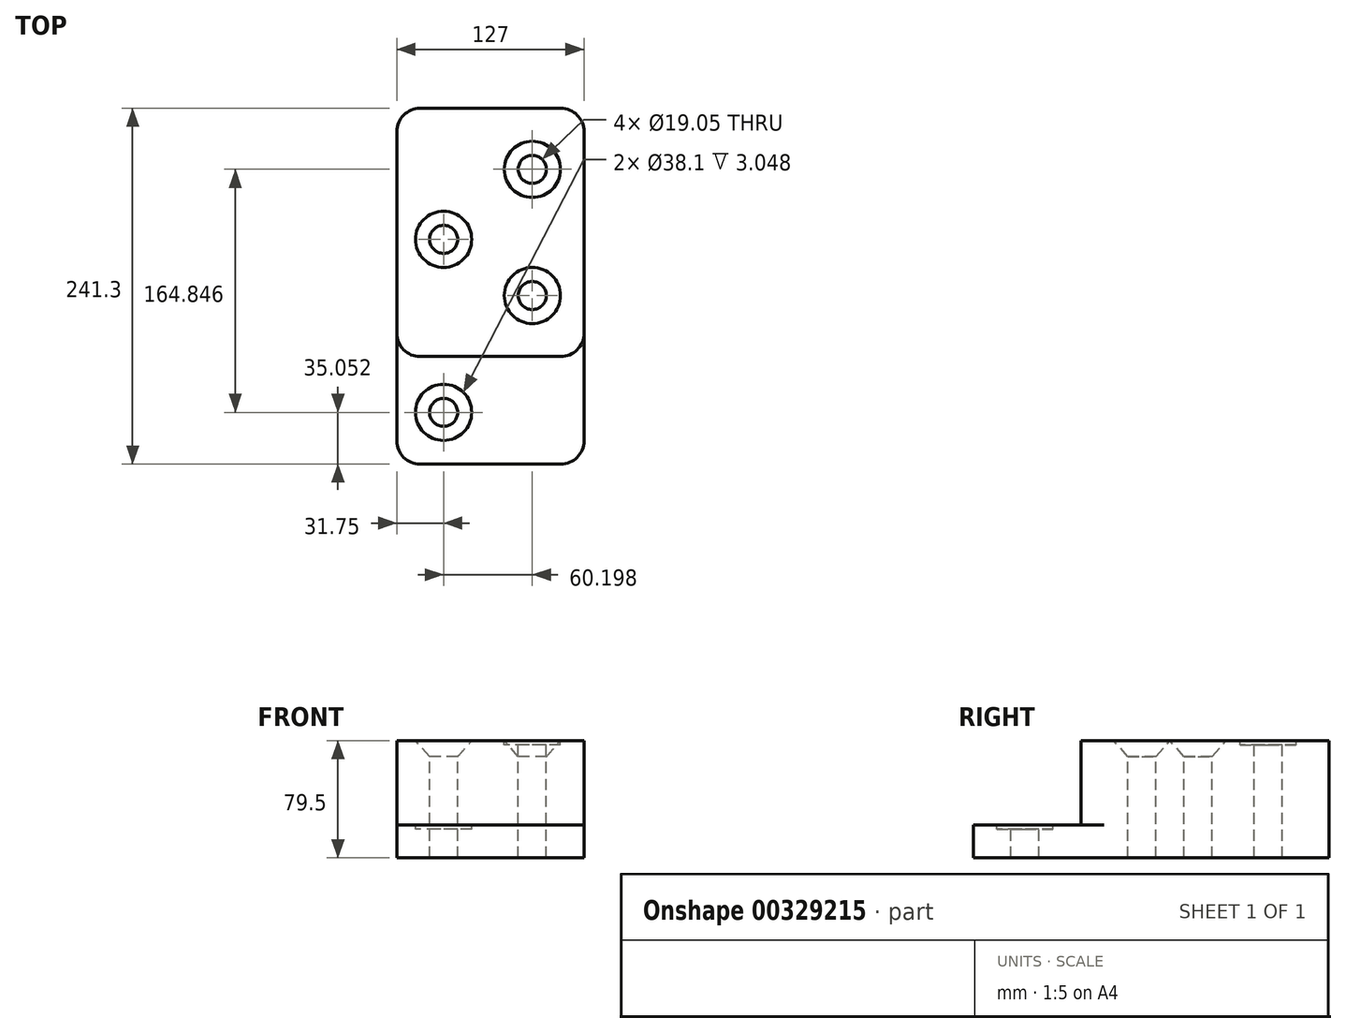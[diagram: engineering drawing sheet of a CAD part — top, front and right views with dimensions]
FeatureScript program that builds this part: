
annotation { "Feature Type Name" : "Feature", "Feature Type Description" : "" }
export const myFeature = defineFeature(function(context is Context, id is Id, definition is map)
    precondition{}
    {
        {
            var Q0;
            Q0=qCreatedBy(makeId("Right.planeOp"),FACE);
            var sketch = newSketch(context, id + "F0", { "sketchPlane" : qUnion([Q0])});
            skLineSegment(sketch, "E0", {"start": v(0, 0) * mm, "end": v(0, 22.35) * mm});
            skLineSegment(sketch, "E1", {"start": v(0, 22.35) * mm, "end": v(72.9, 22.35) * mm});
            skLineSegment(sketch, "E2", {"start": v(72.9, 22.35) * mm, "end": v(72.9, 79.5) * mm});
            skLineSegment(sketch, "E3", {"start": v(72.9, 79.5) * mm, "end": v(241.3, 79.5) * mm});
            skLineSegment(sketch, "E4", {"start": v(241.3, 79.5) * mm, "end": v(241.3, 0) * mm});
            skLineSegment(sketch, "E5", {"start": v(241.3, 0) * mm, "end": v(0, 0) * mm});
            skSolve(sketch);
        }
        {
            var Q0;
            Q0=makeQuery(id+"F0.imprint","IMPRINT",FACE,{"disambiguationData":[TD([[makeQuery(id+"F0.imprint","IMPRINT",EDGE,{"derivedFrom":sQuery(id+"F0.wireOp",EDGE,"E0")}),-1.0]])]});
            extrude(context, id + "F1", {"entities" : qUnion([Q0]), "depth" : 127 * mm});
        }
        {
            var Q0;
            Q0=makeQuery(id+"F1.opExtrude","SWEPT_FACE",FACE,{"disambiguationData":[OSD([sQuery(id+"F0.wireOp",EDGE,"E3")])]});
            var sketch = newSketch(context, id + "F2", { "sketchPlane" : qUnion([Q0])});
            skPoint(sketch, "E6", {"position": v(31.75, 152.4) * mm});
            skPoint(sketch, "E7", {"position": v(91.95, 199.9) * mm});
            skPoint(sketch, "E8", {"position": v(91.95, 114.3) * mm});
            skPoint(sketch, "E9", {"position": v(31.75, 35.05) * mm});
            skSolve(sketch);
        }
        {
            var Q0;
            Q0=sQuery(id+"F2.wireOp",VERTEX,"E6");
            var Q1;
            Q1=sQuery(id+"F2.wireOp",VERTEX,"E8");
            var Q2;
            Q2=makeQuery(id+"F1.opExtrude","SWEPT_BODY",BODY,{"disambiguationData":[OSD([sQuery(id+"F0.wireOp",EDGE,"E0"),sQuery(id+"F0.wireOp",EDGE,"E1"),sQuery(id+"F0.wireOp",EDGE,"E2"),sQuery(id+"F0.wireOp",EDGE,"E3"),sQuery(id+"F0.wireOp",EDGE,"E4"),sQuery(id+"F0.wireOp",EDGE,"E5")])]});
            hole(context, id + "F3", {"style" : HoleStyle.C_SINK, "endStyle" : HoleEndStyle.THROUGH, "holeDiameter" : 19.05 * mm, "cSinkDiameter" : 38.1 * mm, "cSinkAngle" : 82 * degree, "tappedDepth" : 12.7 * mm, "tapClearance" : 3, "locations" : qUnion([Q0, Q1]), "scope" : qUnion([Q2])});
        }
        {
            var Q0;
            Q0=sQuery(id+"F2.wireOp",VERTEX,"E9");
            var Q1;
            Q1=sQuery(id+"F2.wireOp",VERTEX,"E7");
            var Q2;
            Q2=makeQuery(id+"F1.opExtrude","SWEPT_BODY",BODY,{"disambiguationData":[OSD([sQuery(id+"F0.wireOp",EDGE,"E0"),sQuery(id+"F0.wireOp",EDGE,"E1"),sQuery(id+"F0.wireOp",EDGE,"E2"),sQuery(id+"F0.wireOp",EDGE,"E3"),sQuery(id+"F0.wireOp",EDGE,"E4"),sQuery(id+"F0.wireOp",EDGE,"E5")])]});
            hole(context, id + "F4", {"style" : HoleStyle.C_BORE, "endStyle" : HoleEndStyle.THROUGH, "holeDiameter" : 19.05 * mm, "cBoreDiameter" : 38.1 * mm, "cBoreDepth" : 3.05 * mm, "tappedDepth" : 12.7 * mm, "tapClearance" : 3, "locations" : qUnion([Q0, Q1]), "scope" : qUnion([Q2])});
        }
        {
            var Q0;
            Q0=makeQuery(id+"F1.opExtrude","CAP_EDGE",EDGE,{"disambiguationData":[OSD([sQuery(id+"F0.wireOp",EDGE,"E2")])],"isStart":false});
            var Q1;
            Q1=makeQuery(id+"F1.opExtrude","CAP_EDGE",EDGE,{"disambiguationData":[OSD([sQuery(id+"F0.wireOp",EDGE,"E2")])],"isStart":true});
            var Q2;
            Q2=makeQuery(id+"F1.opExtrude","CAP_EDGE",EDGE,{"disambiguationData":[OSD([sQuery(id+"F0.wireOp",EDGE,"E0")])],"isStart":false});
            var Q3;
            Q3=makeQuery(id+"F1.opExtrude","CAP_EDGE",EDGE,{"disambiguationData":[OSD([sQuery(id+"F0.wireOp",EDGE,"E0")])],"isStart":true});
            var Q4;
            Q4=makeQuery(id+"F1.opExtrude","CAP_EDGE",EDGE,{"disambiguationData":[OSD([sQuery(id+"F0.wireOp",EDGE,"E4")])],"isStart":false});
            var Q5;
            Q5=makeQuery(id+"F1.opExtrude","CAP_EDGE",EDGE,{"disambiguationData":[OSD([sQuery(id+"F0.wireOp",EDGE,"E4")])],"isStart":true});
            fillet(context, id + "F5", {"entities" : qUnion([Q0, Q1, Q2, Q3, Q4, Q5]), "radius" : 15.75 * mm, "tangentPropagation" : true, "allowEdgeOverflow" : false});
        }
    });
